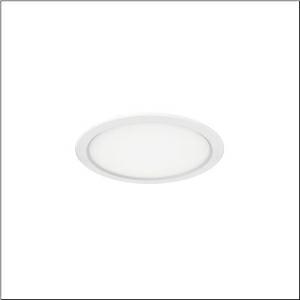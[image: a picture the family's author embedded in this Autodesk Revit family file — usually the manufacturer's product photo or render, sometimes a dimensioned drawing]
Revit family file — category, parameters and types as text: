
# Revit family: lunis_41_eco_51ds107f34a
name_source: partatom
category: Lighting Fixtures
units: mm (PartAtom-declared; Revit-internal decimal feet)

## family parameters
Cut with Voids When Loaded = No
Host = Face
Light Source = No
Part Type = Normal
Room Calculation Point = No
Round Connector Dimension = Use Diameter
Shared = No

## types (1)
- Lunis 41 ECO (1 x LED, 2200 lm, 22 W, 3000K)
    Apparent Load = 22 VA
    CIE Flux Codes = 47 80 97 100 100
    Color Rendering = 80
    Color Temperature = 3000K
    Default Elevation = 1800 mm
    Description = Lunis 41,  ECO, downlight, light emission: direct distribution, LED rated luminous flux: 2.200lm, light colour: 830, control gear: ECG, mains connection: 230V, AC, 50/60Hz, housing, round, of aluminium, coated, traffic white (RAL 9016), diameter: 216mm, recess depth: 58mm, protection rating (complete): IP20, insulation class (complete): insulation class II (safety insulation), certification: CE, permissible ambient temperature for indoor applications: -20..+40°C, packaging unit: 1 piece
    Height = 0 mm  [stored 0 ft]
    Lamp = 1 x LED
    Lamp Light Flux = 2200 lm
    Lamp Power = 22 W
    Lamp count = 1
    Length = 216 mm
    Luminous efficacy = 100 lm/W
    Manufacturer = Siteco
    ModVariant = No
    Model = 51DS107F34A
    Mounting Place = Ceiling
    Mounting Type = Recessed
    Number of Poles = 1
    OnlyDefault = Yes
    Power Factor = 1
    Product Name = Lunis 41 ECO
    Product group = downlight | ceiling recessed
    ProductGroupID = 402
    Protection Class = Protection class II
    Protection Degree = IP 20
    RLX_Detail_Level = 1
    RlxData = <blob elided: 22473 chars, md5=e6544e13>
    Socket = socket
    Standby Power = 0 W
    System Light Flux = 2200 lm
    System Power = 22 W
    Type Comments = Product without accessories
    Type Image = l_1007043.jpg
    URL = http://relux.com
    VarID = ---
    Voltage = 0 V
    Weight = 0.00 kg
    Width = 0 mm  [stored 0 ft]

note: [stored X ft] marks values corroborated as IEEE doubles in the binary element streams (Revit-internal decimal feet)

## geometry (parser evidence)
native form markers: Blend x4, Sweep x10
no freeform markers — native parametric forms only
